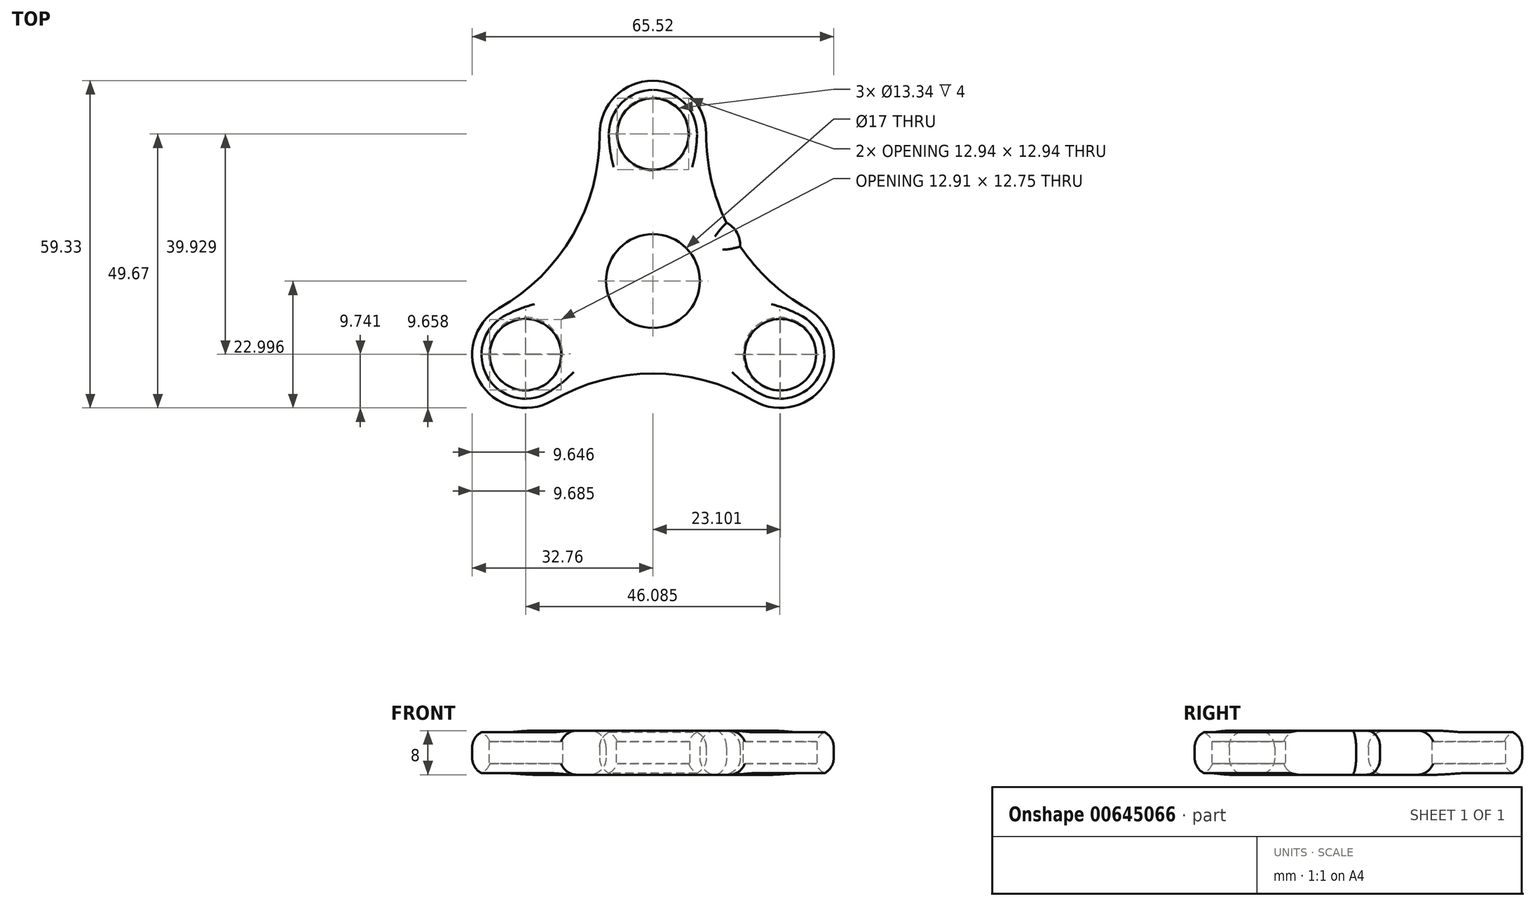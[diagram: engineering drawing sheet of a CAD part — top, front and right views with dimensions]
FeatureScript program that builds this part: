
annotation { "Feature Type Name" : "Feature", "Feature Type Description" : "" }
export const myFeature = defineFeature(function(context is Context, id is Id, definition is map)
    precondition{}
    {
        {
            var Q0;
            Q0=qCreatedBy(makeId("Top.planeOp"),FACE);
            var sketch = newSketch(context, id + "F0", { "sketchPlane" : qUnion([Q0])});
            skCircle(sketch, "E0", {"center": v(0, 0) * mm, "radius": 6.3 * mm});
            skCircle(sketch, "E1", {"center": v(0, 0) * mm, "radius": 9.66 * mm});
            skCircle(sketch, "E2.1.0", {"center": v(-23.1, -40.01) * mm, "radius": 9.66 * mm});
            skCircle(sketch, "E2.1.1", {"center": v(-23.1, -40.01) * mm, "radius": 6.3 * mm});
            skCircle(sketch, "E2.2.0", {"center": v(23.1, -40.01) * mm, "radius": 9.66 * mm});
            skCircle(sketch, "E2.2.1", {"center": v(23.1, -40.01) * mm, "radius": 6.3 * mm});
            skPoint(sketch, "E2.center", {"position": v(0, -26.67) * mm});
            skLineSegment(sketch, "E3", {"start": v(0, 0) * mm, "end": v(-9.66, 0) * mm, "construction": true});
            skCircle(sketch, "E4", {"center": v(0, -26.67) * mm, "radius": 8.5 * mm});
            skLineSegment(sketch, "E5", {"start": v(0, -26.67) * mm, "end": v(-23.1, -40.01) * mm, "construction": true});
            skLineSegment(sketch, "E6", {"start": v(23.1, -40.01) * mm, "end": v(0, -26.67) * mm, "construction": true});
            skLineSegment(sketch, "E7", {"start": v(0, -26.67) * mm, "end": v(0, 0) * mm, "construction": true});
            skLineSegment(sketch, "E8", {"start": v(23.1, -40.01) * mm, "end": v(27.93, -31.64) * mm, "construction": true});
            skLineSegment(sketch, "E9", {"start": v(0, 0) * mm, "end": v(9.66, 0) * mm, "construction": true});
            skLineSegment(sketch, "E10", {"start": v(-23.1, -40.01) * mm, "end": v(-27.93, -31.64) * mm, "construction": true});
            skArc(sketch, "E11", {"start": v(-27.93, -31.64) * mm, "mid": v(-14.5, -18.3) * mm, "end": v(-9.66, 0) * mm});
            skArc(sketch, "E12", {"start": v(9.66, 0) * mm, "mid": v(14.5, -18.3) * mm, "end": v(27.93, -31.64) * mm});
            skLineSegment(sketch, "E13", {"start": v(-23.1, -40.01) * mm, "end": v(-18.27, -48.38) * mm, "construction": true});
            skLineSegment(sketch, "E14", {"start": v(23.1, -40.01) * mm, "end": v(18.27, -48.38) * mm, "construction": true});
            skArc(sketch, "E15", {"start": v(18.27, -48.38) * mm, "mid": v(0, -43.43) * mm, "end": v(-18.27, -48.38) * mm});
            skLineSegment(sketch, "E16", {"start": v(0, -26.67) * mm, "end": v(-14.5, -18.3) * mm, "construction": true});
            skLineSegment(sketch, "E17", {"start": v(-14.5, -18.3) * mm, "end": v(0, -26.67) * mm, "construction": true});
            skLineSegment(sketch, "E18", {"start": v(0, -26.67) * mm, "end": v(14.5, -18.3) * mm, "construction": true});
            skLineSegment(sketch, "E19", {"start": v(0, -26.67) * mm, "end": v(0, -43.43) * mm, "construction": true});
            skLineSegment(sketch, "E20", {"start": v(14.5, -18.3) * mm, "end": v(15.83, -20.42) * mm, "construction": true});
            skLineSegment(sketch, "E21", {"start": v(14.5, -18.3) * mm, "end": v(13.33, -16.1) * mm, "construction": true});
            skArc(sketch, "E22", {"start": v(15.83, -20.42) * mm, "mid": v(15.22, -17.89) * mm, "end": v(13.33, -16.1) * mm});
            skArc(sketch, "E23.MirrorCS", {"start": v(-15.83, -20.42) * mm, "mid": v(-15.22, -17.89) * mm, "end": v(-13.33, -16.1) * mm});
            skArc(sketch, "E24.MirrorCS", {"start": v(2.5, -43.51) * mm, "mid": v(0, -44.25) * mm, "end": v(-2.5, -43.51) * mm});
            skSolve(sketch);
        }
        {
            var Q0;
            Q0=makeQuery(id+"F0.imprint","IMPRINT",FACE,{"disambiguationData":[TD([[makeQuery(id+"F0.imprint","IMPRINT",EDGE,{"derivedFrom":sQuery(id+"F0.wireOp",EDGE,"E0")}),-1.0]])]});
            var Q1;
            Q1=makeQuery(id+"F0.imprint","IMPRINT",FACE,{"disambiguationData":[TD([[makeQuery(id+"F0.imprint","IMPRINT",EDGE,{"derivedFrom":sQuery(id+"F0.wireOp",EDGE,"E2.1.1")}),-1.0]])]});
            var Q2;
            Q2=makeQuery(id+"F0.imprint","IMPRINT",FACE,{"disambiguationData":[TD([[makeQuery(id+"F0.imprint","IMPRINT",EDGE,{"derivedFrom":sQuery(id+"F0.wireOp",EDGE,"E2.2.1")}),-1.0]])]});
            var Q3;
            {var subQ0=sQuery(id+"F0.wireOp",EDGE,"UzU74dU8-enYz-kkmd-C7oZ-pswxIBgTCVmV");var subQ1=sQuery(id+"F0.wireOp",EDGE,"E12");var subQ2=makeQuery(id+"F0.imprint","INTERSECT",VERTEX,{"disambiguationData":[OD(1.0)],"derivedFrom":[subQ1,subQ0]});Q3=makeQuery(id+"F0.imprint","IMPRINT",FACE,{"disambiguationData":[TD([[makeQuery(id+"F0.imprint","IMPRINT",EDGE,{"disambiguationData":[TD([[subQ2,-1.0]])],"derivedFrom":subQ1}),1.0]])]});}
            var Q4;
            {var subQ0=sQuery(id+"F0.wireOp",EDGE,"d11itaW9-BDd3-fUXO-ILgY-40LG9F4n92Nl");var subQ1=sQuery(id+"F0.wireOp",EDGE,"E12");var subQ2=makeQuery(id+"F0.imprint","INTERSECT",VERTEX,{"disambiguationData":[OD(1.0)],"derivedFrom":[subQ1,subQ0]});Q4=makeQuery(id+"F0.imprint","IMPRINT",FACE,{"disambiguationData":[TD([[makeQuery(id+"F0.imprint","IMPRINT",EDGE,{"disambiguationData":[TD([[subQ2,-1.0]])],"derivedFrom":subQ1}),1.0]])]});}
            var Q5;
            Q5=makeQuery(id+"F0.imprint","IMPRINT",FACE,{"disambiguationData":[TD([[makeQuery(id+"F0.imprint","IMPRINT",EDGE,{"derivedFrom":sQuery(id+"F0.wireOp",EDGE,"E4")}),-1.0]])]});
            var Q6;
            {var subQ0=sQuery(id+"F0.wireOp",EDGE,"E22");Q6=makeQuery(id+"F0.imprint","IMPRINT",FACE,{"disambiguationData":[TD([[makeQuery(id+"F0.imprint","IMPRINT",EDGE,{"derivedFrom":subQ0}),1.0]])]});}
            var Q7;
            {var subQ0=sQuery(id+"F0.wireOp",EDGE,"E23.MirrorCS");Q7=makeQuery(id+"F0.imprint","IMPRINT",FACE,{"disambiguationData":[TD([[makeQuery(id+"F0.imprint","IMPRINT",EDGE,{"derivedFrom":subQ0}),-1.0]])]});}
            var Q8;
            {var subQ0=sQuery(id+"F0.wireOp",EDGE,"E24.MirrorCS");Q8=makeQuery(id+"F0.imprint","IMPRINT",FACE,{"disambiguationData":[TD([[makeQuery(id+"F0.imprint","IMPRINT",EDGE,{"derivedFrom":subQ0}),-1.0]])]});}
            extrude(context, id + "F1", {"entities" : qUnion([Q0, Q1, Q2, Q3, Q4, Q5, Q6, Q7, Q8]), "depth" : 8 * mm, "offsetDistance" : 25 * mm});
        }
        {
            var Q0;
            Q0=makeQuery(id+"F1.opExtrude","CAP_FACE",FACE,{"disambiguationData":[OSD([sQuery(id+"F0.wireOp",EDGE,"E0"),sQuery(id+"F0.wireOp",EDGE,"E1"),sQuery(id+"F0.wireOp",EDGE,"E2.1.0"),sQuery(id+"F0.wireOp",EDGE,"E2.1.1"),sQuery(id+"F0.wireOp",EDGE,"E2.2.0"),sQuery(id+"F0.wireOp",EDGE,"E2.2.1"),sQuery(id+"F0.wireOp",EDGE,"E4"),sQuery(id+"F0.wireOp",EDGE,"E11"),sQuery(id+"F0.wireOp",EDGE,"E12"),sQuery(id+"F0.wireOp",EDGE,"E15")])],"isStart":true});
            fillet(context, id + "F2", {"entities" : qUnion([Q0]), "radius" : 3 * mm, "tangentPropagation" : true, "allowEdgeOverflow" : false});
        }
        {
            var Q0;
            Q0=makeQuery(id+"F1.opExtrude","CAP_FACE",FACE,{"disambiguationData":[OSD([sQuery(id+"F0.wireOp",EDGE,"E0"),sQuery(id+"F0.wireOp",EDGE,"E1"),sQuery(id+"F0.wireOp",EDGE,"E2.1.0"),sQuery(id+"F0.wireOp",EDGE,"E2.1.1"),sQuery(id+"F0.wireOp",EDGE,"E2.2.0"),sQuery(id+"F0.wireOp",EDGE,"E2.2.1"),sQuery(id+"F0.wireOp",EDGE,"E4"),sQuery(id+"F0.wireOp",EDGE,"E11"),sQuery(id+"F0.wireOp",EDGE,"E12"),sQuery(id+"F0.wireOp",EDGE,"E15")])],"isStart":false});
            fillet(context, id + "F3", {"entities" : qUnion([Q0]), "radius" : 3 * mm, "tangentPropagation" : true, "allowEdgeOverflow" : false});
        }
        {
            var Q0;
            Q0=qCreatedBy(makeId("Right.planeOp"),FACE);
            var sketch = newSketch(context, id + "F4", { "sketchPlane" : qUnion([Q0])});
            skLineSegment(sketch, "E25", {"start": v(18.83, 0) * mm, "end": v(18.83, 4) * mm, "construction": true});
            skSolve(sketch);
        }
        {
            var Q0;
            Q0=sQuery(id+"F4.wireOp",EDGE,"E25");
            cPlane(context, id + "F5", {"entities" : qUnion([Q0]), "cplaneType" : CPlaneType.MID_PLANE, "offset" : 25 * mm, "width" : 150 * mm, "height" : 150 * mm});
        }
        {
            var Q0;
            Q0=qCreatedBy(id+"F5.planeOp",FACE);
            var sketch = newSketch(context, id + "F6", { "sketchPlane" : qUnion([Q0])});
            skCircle(sketch, "E26", {"center": v(0, 0) * mm, "radius": 6.67 * mm});
            skCircle(sketch, "E27.1.0", {"center": v(-23.07, -39.9) * mm, "radius": 6.67 * mm});
            skCircle(sketch, "E27.2.0", {"center": v(23.01, -39.93) * mm, "radius": 6.67 * mm});
            skPoint(sketch, "E27.center", {"position": v(-0.02, -26.6) * mm});
            skSolve(sketch);
        }
        {
            var Q0;
            Q0=qSketchRegion(id+"F6",true);
            extrude(context, id + "F7", {"entities" : qUnion([Q0]), "operationType" : NewBodyOperationType.REMOVE, "depth" : 4 * mm, "offsetDistance" : 25 * mm});
        }
    });
